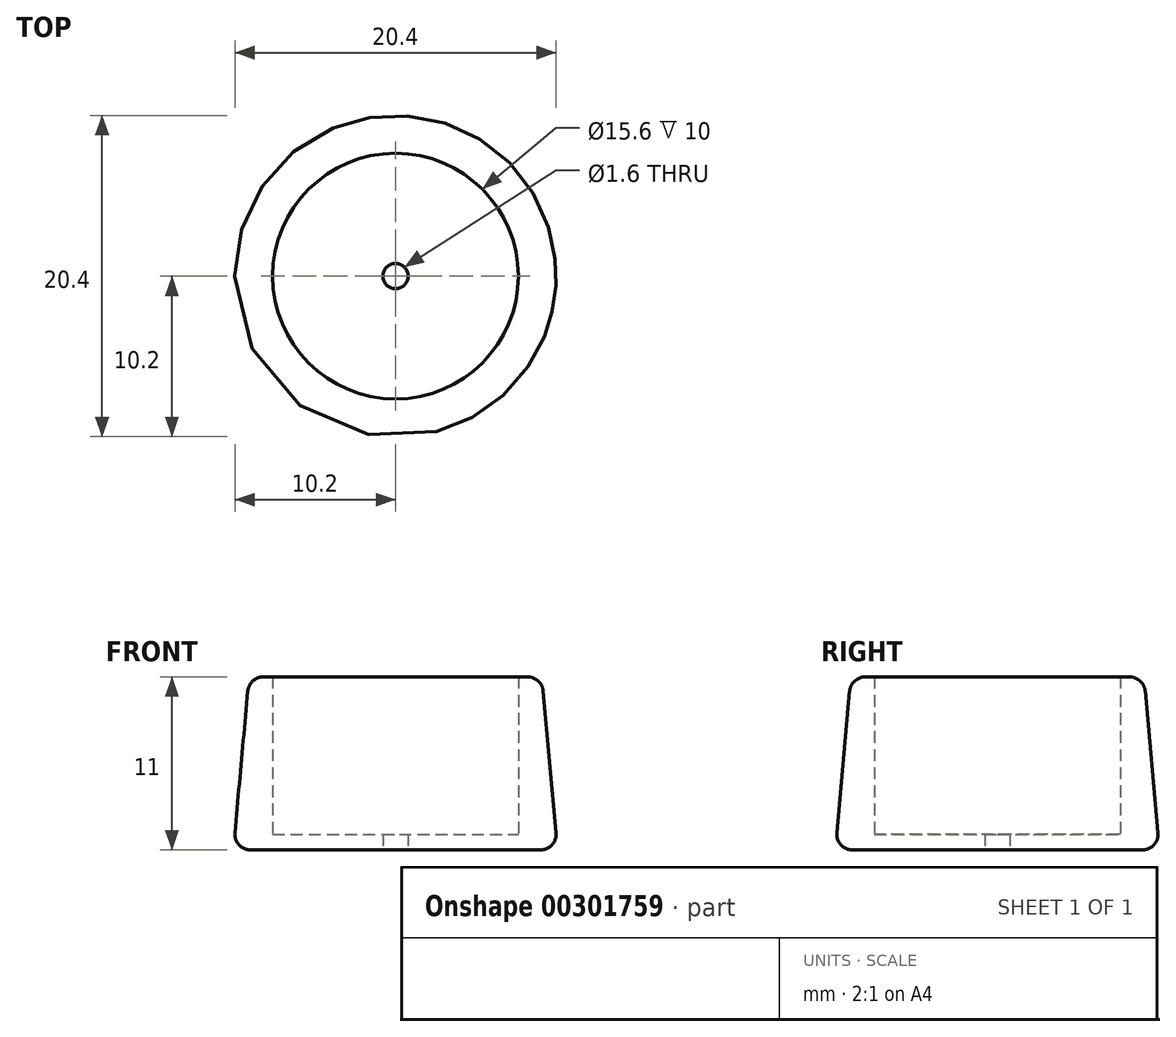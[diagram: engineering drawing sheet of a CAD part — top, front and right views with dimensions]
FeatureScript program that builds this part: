
annotation { "Feature Type Name" : "Feature", "Feature Type Description" : "" }
export const myFeature = defineFeature(function(context is Context, id is Id, definition is map)
    precondition{}
    {
        {
            var Q0;
            Q0=qCreatedBy(makeId("Front.planeOp"),FACE);
            var sketch = newSketch(context, id + "F0", { "sketchPlane" : qUnion([Q0])});
            skLineSegment(sketch, "E0", {"start": v(-0.8, 0) * mm, "end": v(-9.2, 0) * mm});
            skLineSegment(sketch, "E1", {"start": v(-10.2, 1.1) * mm, "end": v(-9.38, 10.1) * mm});
            skLineSegment(sketch, "E2", {"start": v(-8.39, 11) * mm, "end": v(-7.8, 11) * mm});
            skLineSegment(sketch, "E3", {"start": v(-7.8, 11) * mm, "end": v(-7.8, 1) * mm});
            skLineSegment(sketch, "E4", {"start": v(-7.8, 1) * mm, "end": v(-0.8, 1) * mm});
            skLineSegment(sketch, "E5", {"start": v(-0.8, 1) * mm, "end": v(-0.8, 0) * mm});
            skLineSegment(sketch, "E6", {"start": v(-9.3, 11) * mm, "end": v(-9.3, 0) * mm, "construction": true});
            skPoint(sketch, "E7.visualSharp", {"position": v(-10.3, 0) * mm});
            skArc(sketch, "E7.filletArc", {"start": v(-10.2, 1.1) * mm, "mid": v(-9.94, 0.33) * mm, "end": v(-9.2, 0) * mm});
            skPoint(sketch, "E8.visualSharp", {"position": v(-9.3, 11) * mm});
            skArc(sketch, "E8.filletArc", {"start": v(-8.39, 11) * mm, "mid": v(-9.06, 10.74) * mm, "end": v(-9.38, 10.1) * mm});
            skLineSegment(sketch, "E9", {"start": v(0, 0) * mm, "end": v(0, 2.63) * mm, "construction": true});
            skSolve(sketch);
        }
        {
            var Q0;
            Q0=makeQuery(id+"F0.imprint","IMPRINT",FACE,{"disambiguationData":[TD([[makeQuery(id+"F0.imprint","IMPRINT",EDGE,{"derivedFrom":sQuery(id+"F0.wireOp",EDGE,"E0")}),-1.0]])]});
            var Q1;
            Q1=sQuery(id+"F0.wireOp",EDGE,"E9");
            revolve(context, id + "F1", {"entities" : qUnion([Q0]), "axis" : qUnion([Q1]), "revolveType" : RevolveType.FULL});
        }
    });
